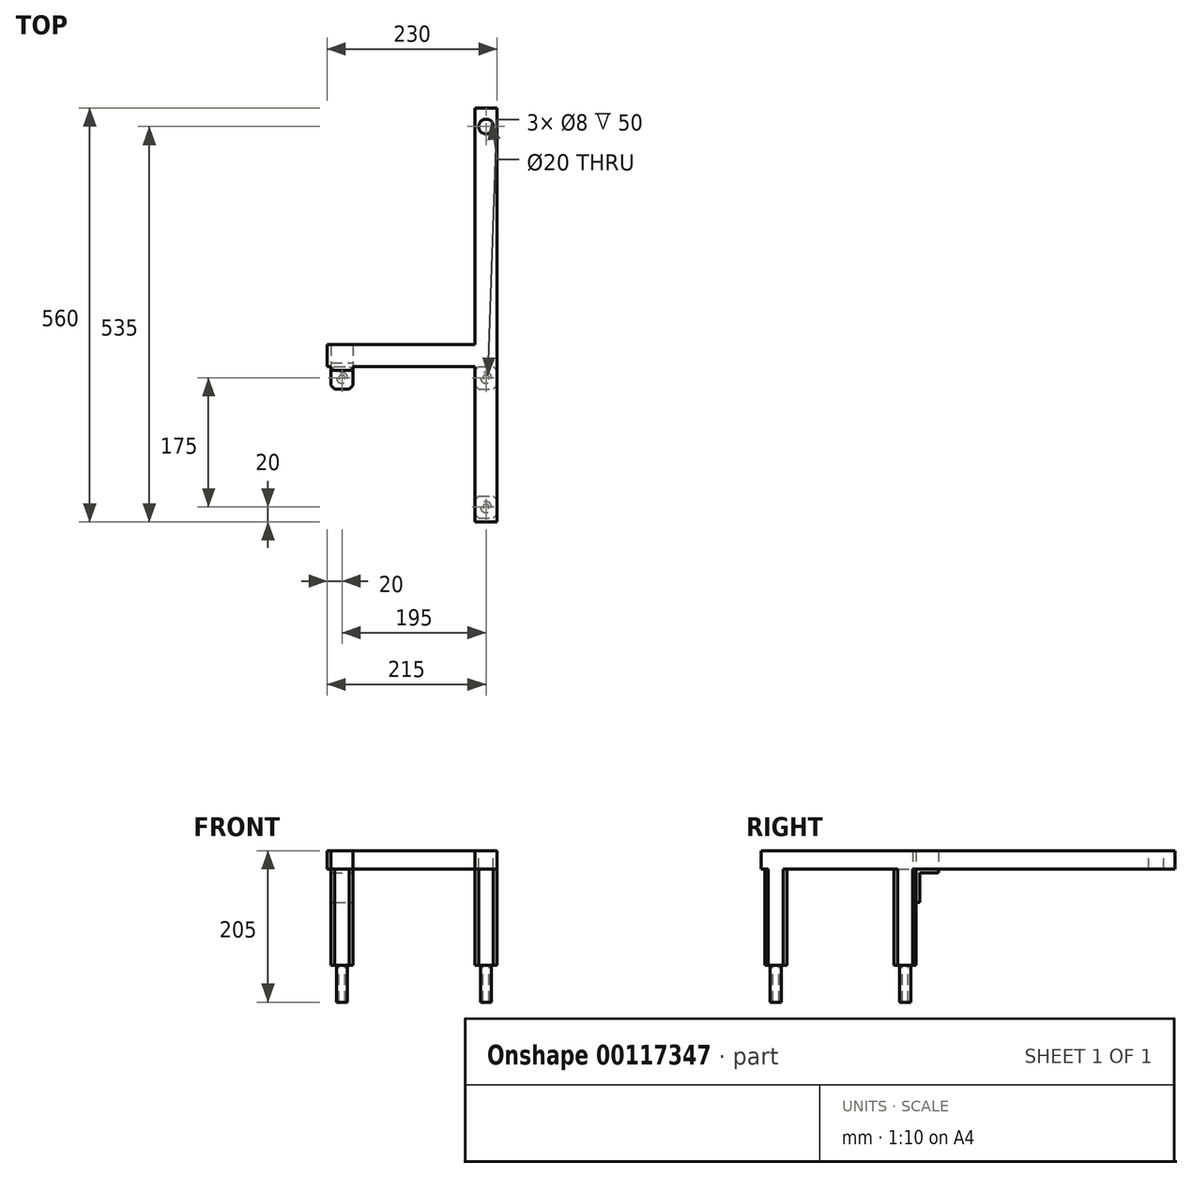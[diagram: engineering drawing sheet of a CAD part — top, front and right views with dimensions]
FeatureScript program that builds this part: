
annotation { "Feature Type Name" : "Feature", "Feature Type Description" : "" }
export const myFeature = defineFeature(function(context is Context, id is Id, definition is map)
    precondition{}
    {
        {
            var Q0;
            Q0=qCreatedBy(makeId("Front.planeOp"),FACE);
            var sketch = newSketch(context, id + "F0", { "sketchPlane" : qUnion([Q0])});
            skLineSegment(sketch, "E0.bottom", {"start": v(15, -12.5) * mm, "end": v(-15, -12.5) * mm});
            skLineSegment(sketch, "E0.top", {"start": v(15, 12.5) * mm, "end": v(-15, 12.5) * mm});
            skLineSegment(sketch, "E0.left", {"start": v(15, -12.5) * mm, "end": v(15, 12.5) * mm});
            skLineSegment(sketch, "E0.right", {"start": v(-15, -12.5) * mm, "end": v(-15, 12.5) * mm});
            skPoint(sketch, "E0.middle", {"position": v(0, 0) * mm});
            skSolve(sketch);
        }
        {
            var Q0;
            Q0 = qSketchRegion(id + "F0", true);
            extrude(context, id + "F1", {"entities" : qUnion([Q0]), "depth" : 560 * mm});
        }
        {
            var Q0;
            Q0=makeQuery(id+"F1.opExtrude","SWEPT_FACE",FACE,{"disambiguationData":[OSD([sQuery(id+"F0.wireOp",EDGE,"E0.right")])]});
            var sketch = newSketch(context, id + "F2", { "sketchPlane" : qUnion([Q0])});
            skLineSegment(sketch, "E1.bottom", {"start": v(320, 12.5) * mm, "end": v(350, 12.5) * mm});
            skLineSegment(sketch, "E1.top", {"start": v(320, -12.5) * mm, "end": v(350, -12.5) * mm});
            skLineSegment(sketch, "E1.left", {"start": v(320, 12.5) * mm, "end": v(320, -12.5) * mm});
            skLineSegment(sketch, "E1.right", {"start": v(350, 12.5) * mm, "end": v(350, -12.5) * mm});
            skSolve(sketch);
        }
        {
            var Q0;
            Q0 = qSketchRegion(id + "F2", true);
            extrude(context, id + "F3", {"entities" : qUnion([Q0]), "operationType" : NewBodyOperationType.ADD, "depth" : 200 * mm});
        }
        {
            var Q0;
            Q0=makeQuery(id+"F3.boolean.opBoolean","MERGE",FACE,{"derivedFrom":[makeQuery(id+"F1.opExtrude","SWEPT_FACE",FACE,{"disambiguationData":[OSD([sQuery(id+"F0.wireOp",EDGE,"E0.top")])]}),makeQuery(id+"F3.opExtrude","SWEPT_FACE",FACE,{"disambiguationData":[OSD([sQuery(id+"F2.wireOp",EDGE,"E1.bottom")])]})]});
            var sketch = newSketch(context, id + "F4", { "sketchPlane" : qUnion([Q0])});
            skCircle(sketch, "E2", {"center": v(0, -25) * mm, "radius": 10 * mm});
            skSolve(sketch);
        }
        {
            var Q0;
            Q0 = qSketchRegion(id + "F4", true);
            extrude(context, id + "F5", {"entities" : qUnion([Q0]), "operationType" : NewBodyOperationType.REMOVE, "oppositeDirection" : true, "depth" : 25 * mm});
        }
        {
            var Q0;
            Q0=makeQuery(id+"F3.boolean.opBoolean","MERGE",FACE,{"derivedFrom":[makeQuery(id+"F1.opExtrude","SWEPT_FACE",FACE,{"disambiguationData":[OSD([sQuery(id+"F0.wireOp",EDGE,"E0.bottom")])]}),makeQuery(id+"F3.opExtrude","SWEPT_FACE",FACE,{"disambiguationData":[OSD([sQuery(id+"F2.wireOp",EDGE,"E1.top")])]})]});
            var sketch = newSketch(context, id + "F6", { "sketchPlane" : qUnion([Q0])});
            skLineSegment(sketch, "E3.bottom", {"start": v(-15, 525) * mm, "end": v(15, 525) * mm});
            skLineSegment(sketch, "E3.top", {"start": v(-15, 555) * mm, "end": v(15, 555) * mm});
            skLineSegment(sketch, "E3.left", {"start": v(-15, 525) * mm, "end": v(-15, 555) * mm});
            skLineSegment(sketch, "E3.right", {"start": v(15, 525) * mm, "end": v(15, 555) * mm});
            skLineSegment(sketch, "E4.bottom", {"start": v(-15, 350) * mm, "end": v(15, 350) * mm});
            skLineSegment(sketch, "E4.top", {"start": v(-15, 380) * mm, "end": v(15, 380) * mm});
            skLineSegment(sketch, "E4.left", {"start": v(-15, 350) * mm, "end": v(-15, 380) * mm});
            skLineSegment(sketch, "E4.right", {"start": v(15, 350) * mm, "end": v(15, 380) * mm});
            skSolve(sketch);
        }
        {
            var Q0;
            Q0 = qSketchRegion(id + "F6", true);
            extrude(context, id + "F7", {"entities" : qUnion([Q0]), "operationType" : NewBodyOperationType.ADD, "depth" : 130 * mm});
        }
        {
            var Q0;
            Q0=makeQuery(id+"F7.opExtrude","SWEPT_EDGE",EDGE,{"disambiguationData":[OSD([sQuery(id+"F0.wireOp",EDGE,"E0.bottom"),sQuery(id+"F0.wireOp",EDGE,"E0.right"),sQuery(id+"F2.wireOp",EDGE,"E1.top"),sQuery(id+"F2.wireOp",EDGE,"E1.right"),sQuery(id+"F6.wireOp",EDGE,"hilKdUUq-RNRd-S9px-SIMT-pQA7PgdQDnr3.bottom"),sQuery(id+"F6.wireOp",EDGE,"hilKdUUq-RNRd-S9px-SIMT-pQA7PgdQDnr3.left")])]});
            var Q1;
            Q1=makeQuery(id+"F7.opExtrude","SWEPT_EDGE",EDGE,{"disambiguationData":[OSD([sQuery(id+"F0.wireOp",EDGE,"E0.bottom"),sQuery(id+"F0.wireOp",EDGE,"E0.right"),sQuery(id+"F2.wireOp",EDGE,"E1.top"),sQuery(id+"F2.wireOp",EDGE,"E1.right"),sQuery(id+"F6.wireOp",EDGE,"hilKdUUq-RNRd-S9px-SIMT-pQA7PgdQDnr3.bottom"),sQuery(id+"F6.wireOp",EDGE,"hilKdUUq-RNRd-S9px-SIMT-pQA7PgdQDnr3.right")])]});
            var Q2;
            Q2=makeQuery(id+"F7.opExtrude","SWEPT_EDGE",EDGE,{"disambiguationData":[OSD([sQuery(id+"F0.wireOp",EDGE,"E0.bottom"),sQuery(id+"F0.wireOp",EDGE,"E0.right"),sQuery(id+"F2.wireOp",EDGE,"E1.top"),sQuery(id+"F2.wireOp",EDGE,"E1.left"),sQuery(id+"F6.wireOp",EDGE,"hilKdUUq-RNRd-S9px-SIMT-pQA7PgdQDnr3.top"),sQuery(id+"F6.wireOp",EDGE,"hilKdUUq-RNRd-S9px-SIMT-pQA7PgdQDnr3.left")])]});
            var Q3;
            Q3=makeQuery(id+"F7.opExtrude","SWEPT_EDGE",EDGE,{"disambiguationData":[OSD([sQuery(id+"F0.wireOp",EDGE,"E0.bottom"),sQuery(id+"F0.wireOp",EDGE,"E0.right"),sQuery(id+"F2.wireOp",EDGE,"E1.top"),sQuery(id+"F2.wireOp",EDGE,"E1.left"),sQuery(id+"F6.wireOp",EDGE,"hilKdUUq-RNRd-S9px-SIMT-pQA7PgdQDnr3.top"),sQuery(id+"F6.wireOp",EDGE,"hilKdUUq-RNRd-S9px-SIMT-pQA7PgdQDnr3.right")])]});
            var Q4;
            Q4=makeQuery(id+"F7.opExtrude","SWEPT_EDGE",EDGE,{"disambiguationData":[OSD([sQuery(id+"F0.wireOp",EDGE,"E0.bottom"),sQuery(id+"F0.wireOp",EDGE,"E0.right"),sQuery(id+"F6.wireOp",EDGE,"E3.top"),sQuery(id+"F6.wireOp",EDGE,"E3.left")])]});
            var Q5;
            Q5=makeQuery(id+"F7.opExtrude","SWEPT_EDGE",EDGE,{"disambiguationData":[OSD([sQuery(id+"F0.wireOp",EDGE,"E0.bottom"),sQuery(id+"F0.wireOp",EDGE,"E0.left"),sQuery(id+"F6.wireOp",EDGE,"E3.top"),sQuery(id+"F6.wireOp",EDGE,"E3.right")])]});
            var Q6;
            Q6=makeQuery(id+"F7.opExtrude","SWEPT_EDGE",EDGE,{"disambiguationData":[OSD([sQuery(id+"F0.wireOp",EDGE,"E0.bottom"),sQuery(id+"F0.wireOp",EDGE,"E0.left"),sQuery(id+"F6.wireOp",EDGE,"E3.bottom"),sQuery(id+"F6.wireOp",EDGE,"E3.right")])]});
            var Q7;
            Q7=makeQuery(id+"F7.opExtrude","SWEPT_EDGE",EDGE,{"disambiguationData":[OSD([sQuery(id+"F0.wireOp",EDGE,"E0.bottom"),sQuery(id+"F0.wireOp",EDGE,"E0.right"),sQuery(id+"F6.wireOp",EDGE,"E3.bottom"),sQuery(id+"F6.wireOp",EDGE,"E3.left")])]});
            chamfer(context, id + "F8", {"entities" : qUnion([Q0, Q1, Q2, Q3, Q4, Q5, Q6, Q7]), "width" : 5 * mm, "tangentPropagation" : true});
        }
        {
            var Q0;
            Q0=makeQuery(id+"F7.opExtrude","CAP_FACE",FACE,{"disambiguationData":[OSD([sQuery(id+"F6.wireOp",EDGE,"E3.bottom"),sQuery(id+"F6.wireOp",EDGE,"E3.top"),sQuery(id+"F6.wireOp",EDGE,"E3.left"),sQuery(id+"F6.wireOp",EDGE,"E3.right")])],"isStart":false});
            var sketch = newSketch(context, id + "F9", { "sketchPlane" : qUnion([Q0])});
            skCircle(sketch, "E5", {"center": v(0, 540) * mm, "radius": 7.5 * mm});
            skPoint(sketch, "E5.centerSnap0", {"position": v(15, 540) * mm});
            skPoint(sketch, "E5.centerSnap1", {"position": v(0, 555) * mm});
            skCircle(sketch, "E6", {"center": v(0, 540) * mm, "radius": 4 * mm});
            skSolve(sketch);
        }
        {
            var Q0;
            Q0 = qSketchRegion(id + "F9", true);
            extrude(context, id + "F10", {"entities" : qUnion([Q0]), "operationType" : NewBodyOperationType.ADD, "depth" : 50 * mm});
        }
        {
            var Q0;
            Q0=makeQuery(id+"F7.opExtrude","SWEPT_EDGE",EDGE,{"disambiguationData":[OSD([sQuery(id+"F0.wireOp",EDGE,"E0.bottom"),sQuery(id+"F0.wireOp",EDGE,"E0.left"),sQuery(id+"F6.wireOp",EDGE,"qV6e69VZ-wRGZ-xGnD-934x-wuSxaYri07n0.bottom"),sQuery(id+"F6.wireOp",EDGE,"qV6e69VZ-wRGZ-xGnD-934x-wuSxaYri07n0.right")])]});
            var Q1;
            Q1=makeQuery(id+"F7.opExtrude","SWEPT_EDGE",EDGE,{"disambiguationData":[OSD([sQuery(id+"F0.wireOp",EDGE,"E0.bottom"),sQuery(id+"F0.wireOp",EDGE,"E0.left"),sQuery(id+"F6.wireOp",EDGE,"qV6e69VZ-wRGZ-xGnD-934x-wuSxaYri07n0.top"),sQuery(id+"F6.wireOp",EDGE,"qV6e69VZ-wRGZ-xGnD-934x-wuSxaYri07n0.right")])]});
            var Q2;
            Q2=makeQuery(id+"F7.opExtrude","SWEPT_EDGE",EDGE,{"disambiguationData":[OSD([sQuery(id+"F0.wireOp",EDGE,"E0.bottom"),sQuery(id+"F0.wireOp",EDGE,"E0.right"),sQuery(id+"F6.wireOp",EDGE,"qV6e69VZ-wRGZ-xGnD-934x-wuSxaYri07n0.top"),sQuery(id+"F6.wireOp",EDGE,"qV6e69VZ-wRGZ-xGnD-934x-wuSxaYri07n0.left")])]});
            chamfer(context, id + "F11", {"entities" : qUnion([Q0, Q1, Q2]), "width" : 5 * mm, "tangentPropagation" : true});
        }
        {
            var Q0;
            Q0=makeQuery(id+"F7.opExtrude","CAP_FACE",FACE,{"disambiguationData":[OSD([sQuery(id+"F6.wireOp",EDGE,"E4.bottom"),sQuery(id+"F6.wireOp",EDGE,"E4.top"),sQuery(id+"F6.wireOp",EDGE,"E4.left"),sQuery(id+"F6.wireOp",EDGE,"E4.right")])],"isStart":false});
            var sketch = newSketch(context, id + "F12", { "sketchPlane" : qUnion([Q0])});
            skCircle(sketch, "E7", {"center": v(0, 365) * mm, "radius": 7.5 * mm});
            skPoint(sketch, "E7.centerSnap0", {"position": v(0, 380) * mm});
            skPoint(sketch, "E7.centerSnap1", {"position": v(-15, 365) * mm});
            skCircle(sketch, "E8", {"center": v(0, 365) * mm, "radius": 4 * mm});
            skSolve(sketch);
        }
        {
            var Q0;
            Q0 = qSketchRegion(id + "F12", true);
            extrude(context, id + "F13", {"entities" : qUnion([Q0]), "operationType" : NewBodyOperationType.ADD, "depth" : 50 * mm});
        }
        {
            var Q0;
            {var subQ0=sQuery(id+"F2.wireOp",EDGE,"E1.left");var subQ4=sQuery(id+"F0.wireOp",EDGE,"E0.bottom");var subQ5=sQuery(id+"F2.wireOp",EDGE,"E1.top");Q0=makeQuery(id+"F7.boolean.opBoolean","SPLIT",FACE,{"disambiguationData":[TD([makeQuery(id+"F3.opExtrude","SWEPT_FACE",FACE,{"disambiguationData":[OSD([subQ0])]})])],"derivedFrom":makeQuery(id+"F3.boolean.opBoolean","MERGE",FACE,{"derivedFrom":[makeQuery(id+"F1.opExtrude","SWEPT_FACE",FACE,{"disambiguationData":[OSD([subQ4])]}),makeQuery(id+"F3.opExtrude","SWEPT_FACE",FACE,{"disambiguationData":[OSD([subQ5])]})]})});}
            var sketch = newSketch(context, id + "F14", { "sketchPlane" : qUnion([Q0])});
            skLineSegment(sketch, "E9.bottom", {"start": v(-210, 320) * mm, "end": v(-180, 320) * mm});
            skLineSegment(sketch, "E9.top", {"start": v(-210, 350) * mm, "end": v(-180, 350) * mm});
            skLineSegment(sketch, "E9.left", {"start": v(-210, 320) * mm, "end": v(-210, 350) * mm});
            skLineSegment(sketch, "E9.right", {"start": v(-180, 320) * mm, "end": v(-180, 350) * mm});
            skSolve(sketch);
        }
        {
            var Q0;
            Q0 = qSketchRegion(id + "F14", true);
            extrude(context, id + "F15", {"entities" : qUnion([Q0]), "operationType" : NewBodyOperationType.ADD, "depth" : 5 * mm});
        }
        {
            var Q0;
            Q0=makeQuery(id+"F15.opExtrude","CAP_FACE",FACE,{"disambiguationData":[OSD([sQuery(id+"F14.wireOp",EDGE,"E9.bottom"),sQuery(id+"F14.wireOp",EDGE,"E9.top"),sQuery(id+"F14.wireOp",EDGE,"E9.left"),sQuery(id+"F14.wireOp",EDGE,"E9.right")])],"isStart":false});
            var sketch = newSketch(context, id + "F16", { "sketchPlane" : qUnion([Q0])});
            skLineSegment(sketch, "E10.bottom", {"start": v(-210, 350) * mm, "end": v(-180, 350) * mm});
            skLineSegment(sketch, "E10.top", {"start": v(-210, 345) * mm, "end": v(-180, 345) * mm});
            skLineSegment(sketch, "E10.left", {"start": v(-210, 350) * mm, "end": v(-210, 345) * mm});
            skLineSegment(sketch, "E10.right", {"start": v(-180, 350) * mm, "end": v(-180, 345) * mm});
            skSolve(sketch);
        }
        {
            var Q0;
            Q0 = qSketchRegion(id + "F16", true);
            extrude(context, id + "F17", {"entities" : qUnion([Q0]), "operationType" : NewBodyOperationType.ADD, "depth" : 40 * mm});
        }
        {
            var Q0;
            Q0=makeQuery(id+"F17.boolean.opBoolean","MERGE",FACE,{"derivedFrom":[makeQuery(id+"F15.boolean.opBoolean","MERGE",FACE,{"derivedFrom":[makeQuery(id+"F3.opExtrude","SWEPT_FACE",FACE,{"disambiguationData":[OSD([sQuery(id+"F2.wireOp",EDGE,"E1.right")])]}),makeQuery(id+"F15.opExtrude","SWEPT_FACE",FACE,{"disambiguationData":[OSD([sQuery(id+"F14.wireOp",EDGE,"E9.top")])]})]}),makeQuery(id+"F17.opExtrude","SWEPT_FACE",FACE,{"disambiguationData":[OSD([sQuery(id+"F16.wireOp",EDGE,"E10.bottom")])]})]});
            var sketch = newSketch(context, id + "F18", { "sketchPlane" : qUnion([Q0])});
            skLineSegment(sketch, "E11.bottom", {"start": v(-210, -12.5) * mm, "end": v(-180, -12.5) * mm});
            skLineSegment(sketch, "E11.top", {"start": v(-210, -142.5) * mm, "end": v(-180, -142.5) * mm});
            skLineSegment(sketch, "E11.left", {"start": v(-210, -12.5) * mm, "end": v(-210, -142.5) * mm});
            skLineSegment(sketch, "E11.right", {"start": v(-180, -12.5) * mm, "end": v(-180, -142.5) * mm});
            skSolve(sketch);
        }
        {
            var Q0;
            Q0 = qSketchRegion(id + "F18", true);
            extrude(context, id + "F19", {"entities" : qUnion([Q0]), "operationType" : NewBodyOperationType.ADD, "depth" : 30 * mm});
        }
        {
            var Q0;
            Q0=makeQuery(id+"F19.opExtrude","CAP_EDGE",EDGE,{"disambiguationData":[OSD([sQuery(id+"F18.wireOp",EDGE,"E11.left")])],"isStart":false});
            var Q1;
            Q1=makeQuery(id+"F19.opExtrude","CAP_EDGE",EDGE,{"disambiguationData":[OSD([sQuery(id+"F18.wireOp",EDGE,"E11.right")])],"isStart":false});
            var Q2;
            Q2=makeQuery(id+"F19.opExtrude","CAP_EDGE",EDGE,{"disambiguationData":[OSD([sQuery(id+"F18.wireOp",EDGE,"E11.right")])],"isStart":true});
            var Q3;
            Q3=makeQuery(id+"F19.opExtrude","CAP_EDGE",EDGE,{"disambiguationData":[OSD([sQuery(id+"F18.wireOp",EDGE,"E11.left")])],"isStart":true});
            chamfer(context, id + "F20", {"entities" : qUnion([Q0, Q1, Q2, Q3]), "width" : 5 * mm, "tangentPropagation" : true});
        }
        {
            var Q0;
            Q0=makeQuery(id+"F19.opExtrude","SWEPT_FACE",FACE,{"disambiguationData":[OSD([sQuery(id+"F18.wireOp",EDGE,"E11.top")])]});
            var sketch = newSketch(context, id + "F21", { "sketchPlane" : qUnion([Q0])});
            skCircle(sketch, "E12", {"center": v(-195, 365) * mm, "radius": 7.5 * mm});
            skPoint(sketch, "E12.centerSnap0", {"position": v(-195, 380) * mm});
            skPoint(sketch, "E12.centerSnap1", {"position": v(-210, 365) * mm});
            skCircle(sketch, "E13", {"center": v(-195, 365) * mm, "radius": 4 * mm});
            skSolve(sketch);
        }
        {
            var Q0;
            Q0 = qSketchRegion(id + "F21", true);
            extrude(context, id + "F22", {"entities" : qUnion([Q0]), "operationType" : NewBodyOperationType.ADD, "depth" : 50 * mm});
        }
        {
            var Q0;
            Q0=makeQuery(id+"F19.opExtrude","SWEPT_FACE",FACE,{"disambiguationData":[OSD([sQuery(id+"F18.wireOp",EDGE,"E11.bottom")])]});
            var sketch = newSketch(context, id + "F23", { "sketchPlane" : qUnion([Q0])});
            skLineSegment(sketch, "E14.bottom", {"start": v(-180, -350) * mm, "end": v(-210, -350) * mm});
            skLineSegment(sketch, "E14.top", {"start": v(-180, -355) * mm, "end": v(-210, -355) * mm});
            skLineSegment(sketch, "E14.left", {"start": v(-180, -350) * mm, "end": v(-180, -355) * mm});
            skLineSegment(sketch, "E14.right", {"start": v(-210, -350) * mm, "end": v(-210, -355) * mm});
            skSolve(sketch);
        }
        {
            var Q0;
            Q0 = qSketchRegion(id + "F23", true);
            extrude(context, id + "F24", {"entities" : qUnion([Q0]), "operationType" : NewBodyOperationType.ADD, "depth" : 25 * mm});
        }
    });
